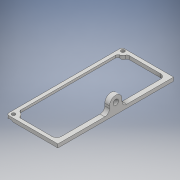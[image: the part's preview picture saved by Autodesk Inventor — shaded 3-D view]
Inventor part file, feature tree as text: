
AUTODESK INVENTOR PART (.ipt)
format: ipt  version: 2018.3 (Build 223284000, 284)  size: 180,224 bytes
history: native  units: mm
features: fillet x4, extrude x3, sketch x3, projected_geometry x1
ambient origin geometry x8: Origin, YZ Plane, XZ Plane, XY Plane, X Axis, Y Axis, Z Axis, Center Point
bodies: Solid1 (feature_tree)
feature tree (11):
  extrude  "Extrusion1"  Depth=3.0mm
  fillet  "Fillet1"  Radius=3.0mm
  fillet  "Fillet2"  Radius=3.0mm
  fillet  "Fillet3"  Radius=3.0mm
  extrude  "Extrusion2"  Depth=2.0mm
  fillet  "Fillet4"  Radius=4.0mm
  extrude  "Extrusion3"  Depth=4.5mm
  sketch  "Sketch1"  dims[d3=3.0mm d4=3.0mm d5=3.0mm d8=3.0mm d11=3.0mm]
  sketch  "Sketch2"  dims[d16=3.0mm d17=0.0mm d18=2.0mm d19=4.0mm]
  projected_geometry  "Projected Loop1"
  sketch  "Sketch3"  dims[d20=2.0mm d21=4.5mm d22=3.0mm d23=9.0mm d24=3.0mm d25=0.0mm d26=4.0mm d27=8.0mm d28=6.0mm d29=3.0mm d30=0.0mm d31=39.5mm d32=43.5mm]
